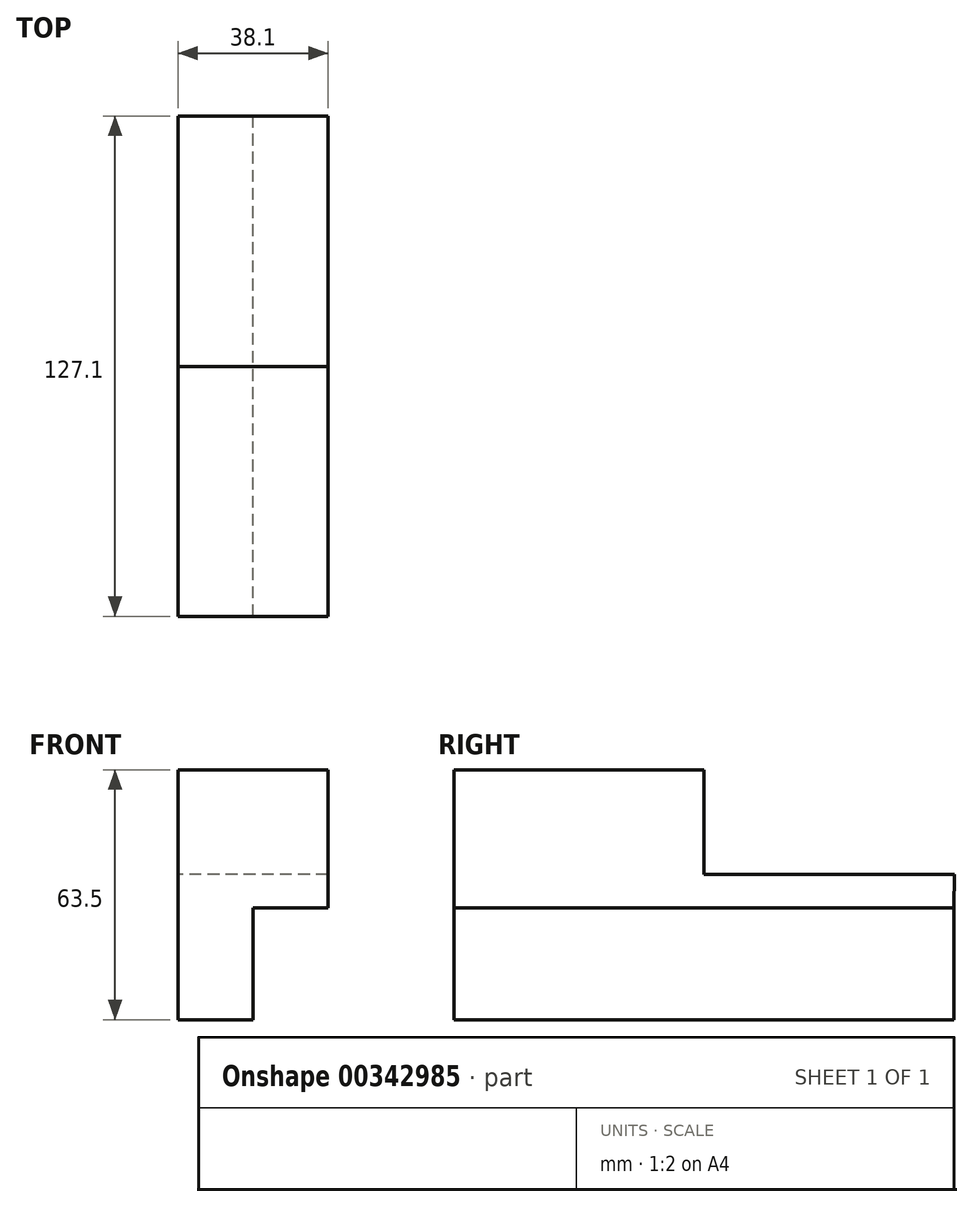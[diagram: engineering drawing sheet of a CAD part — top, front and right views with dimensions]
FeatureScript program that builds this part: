
annotation { "Feature Type Name" : "Feature", "Feature Type Description" : "" }
export const myFeature = defineFeature(function(context is Context, id is Id, definition is map)
    precondition{}
    {
        {
            var Q0;
            Q0=qCreatedBy(makeId("Right.planeOp"),FACE);
            var sketch = newSketch(context, id + "F0", { "sketchPlane" : qUnion([Q0])});
            skLineSegment(sketch, "E0", {"start": v(-65.82, -25.7) * mm, "end": v(61.18, -25.7) * mm});
            skLineSegment(sketch, "E1", {"start": v(-65.82, -25.7) * mm, "end": v(-65.82, 37.8) * mm});
            skLineSegment(sketch, "E2", {"start": v(-65.82, 37.8) * mm, "end": v(-2.32, 37.8) * mm});
            skLineSegment(sketch, "E3", {"start": v(-2.32, 37.8) * mm, "end": v(-2.32, 11.18) * mm});
            skLineSegment(sketch, "E4", {"start": v(-2.32, 11.18) * mm, "end": v(61.28, 11.18) * mm});
            skLineSegment(sketch, "E5", {"start": v(61.28, 11.18) * mm, "end": v(61.18, -25.7) * mm});
            skLineSegment(sketch, "E6", {"start": v(-65.82, 2.76) * mm, "end": v(61.25, 2.76) * mm});
            skSolve(sketch);
        }
        {
            var Q0;
            {var subQ1=sQuery(id+"F0.wireOp",EDGE,"E2");Q0=makeQuery(id+"F0.imprint","IMPRINT",FACE,{"disambiguationData":[TD([[makeQuery(id+"F0.imprint","IMPRINT",EDGE,{"derivedFrom":subQ1}),-1.0]])]});}
            extrude(context, id + "F1", {"entities" : qUnion([Q0]), "depth" : 38.1 * mm});
        }
        {
            var Q0;
            {var subQ0=sQuery(id+"F0.wireOp",EDGE,"E0");Q0=makeQuery(id+"F0.imprint","IMPRINT",FACE,{"disambiguationData":[TD([[makeQuery(id+"F0.imprint","IMPRINT",EDGE,{"derivedFrom":subQ0}),1.0]])]});}
            extrude(context, id + "F2", {"entities" : qUnion([Q0]), "operationType" : NewBodyOperationType.ADD, "depth" : 19.05 * mm});
        }
    });
